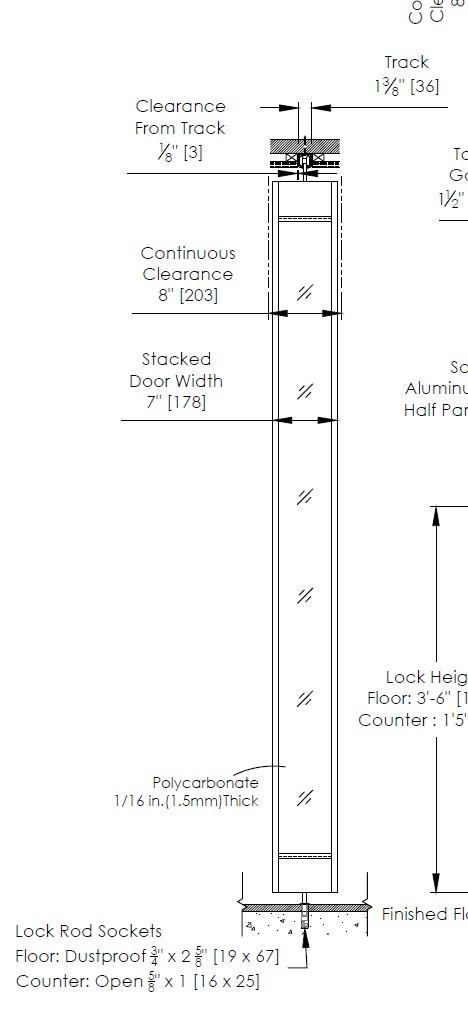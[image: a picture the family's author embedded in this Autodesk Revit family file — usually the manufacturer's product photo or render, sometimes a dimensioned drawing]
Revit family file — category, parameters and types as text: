
# Revit family: Side_Folding_Door_9200-CHI-EZ_Prestige
name_source: partatom
category: Specialty Equipment
units: mm (PartAtom-declared; Revit-internal decimal feet)

## family parameters
Always vertical = Yes
Cut with Voids When Loaded = No
Enable Cutting in Views = No
Maintain Annotation Orientation = No
OmniClass Number = 23.30.10.21
OmniClass Title = Special Function Doors
Part Type = Normal
Room Calculation Point = No
Round Connector Dimension = Use Diameter
Shared = No
Work Plane-Based = No

## types (1)
- EZ - Prestige
    Assembly Code = B2030420
    C Bottom Offset = 0' - 0 3/4"
    C Max Height = 14' - 0"
    C Max Width = 25' - 0"
    C Min Height = 4' - 0"
    C Min Width = 1' - 5 7/8"
    C Panel Width = 0' - 4 1/4"
    C Pocket Width = 0' - 5"
    C Top Gap = 0' - 1 1/2"
    C Track Height = 0' - 1 5/8"
    C Track Thickness = 0' - 0 1/8"
    C Track Width = 0' - 1 3/8"
    Constraints = 1
    Counter = Yes
    Default Elevation = 0' - 0"
    Description = Side-Folding Grille
    Floor = No
    Frame = Metal - Powder Coat - C.H.I Overhead Doors - White
    Glass = Glass - C.H.I Overhead Doors - Frosted
    Keynote = 08330
    Manufacturer = C.H.I. Overhead Doors
    Manufacturer Fax Number = 800-677-2650
    Model = EZ - Prestige
    Product Documentation Link = Contact Manufacturer for More Information
    Product Page URL = Contact Manufacturer for More Information
    URL = https://www.chiohd.com
    Version = 2021-v1.a

## geometry (parser evidence)
native form markers: Sweep x18
no freeform markers — native parametric forms only
